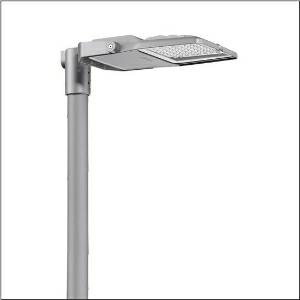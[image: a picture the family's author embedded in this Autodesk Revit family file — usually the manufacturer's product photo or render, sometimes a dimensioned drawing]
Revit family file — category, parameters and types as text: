
# Revit family: floodlight_fl_21_iq_mini___pl43_5xa7772d4a3a_0702
name_source: partatom
category: Lighting Fixtures
units: mm (PartAtom-declared; Revit-internal decimal feet)

## family parameters
Cut with Voids When Loaded = No
Host = Face
Light Source = No
Part Type = Normal
Room Calculation Point = No
Round Connector Dimension = Use Diameter
Shared = No

## types (1)
- --- (1 x LED, 19090 lm, 143 W, 4000K)
    Apparent Load = 143 VA
    CIE Flux Codes = 27 78 99 100 100
    Color Rendering = 70
    Color Temperature = 4000K
    Default Elevation = 1800 mm
    Description = Floodlight FL 21 iQ mini, floodlight, primary light control with lens, of PMMA, primary optical cover: protective disc, of toughened safety glass, transparent, light distribution: PL43, light emission: direct distribution, installation type: surface-mounted, LED, High Power LED, rated luminous flux: 19.090lm, luminous efficacy: 134lm/W, light colour: 740, colour temperature: 4000K, control gear: iQ Street-Remote/DALI, control: Auto-Match, Temp-Guard, Night-Set, Smart-Wire, Desk-Remote (wireless, voltage-free reading and setting of iQ features in the workshop via application-optimized NFC function/RFID function), optimised constant luminous flux control (CLO 2.0), Light-Fading, Lumen-Switch, with terminal, 6-pole, mains connection: 220..240V, AC, 50/60Hz, start of lifetime: 143W, end of service life: 152W, reduction: 61W, luminaire housing, of diecast aluminium, powder-coated, Siteco® metallic grey (DB 702S), corrosivity category C5 mid according to DIN EN ISO 12944, suitable for swimming pools, chlorine-resistant, sealing non-destructively replaceable, please order mast flange separately, mast bracket, of steel, galvanised, powder-coated, protection rating (complete): IP66, insulation class (complete): insulation class II (safety insulation), certification: CE, ENEC, VDE, protection symbol: D, impact resistance: IK08, permissible operating ambient temperature: -40..+40°C, permissible operating ambient temperature for outdoor applications: -40..+50°C, standard: DIN EN 12944, LABS conformity tested according to VDMA 24364:2018-05, packaging unit: 1 piece

Light Distribution: PL43
    Height = 70 mm
    Lamp = 1 x LED
    Lamp Light Flux = 19090 lm
    Lamp Power = 143 W
    Lamp count = 1
    Length = 485 mm
    Luminous efficacy = 133 lm/W
    Manufacturer = Siteco
    ModVariant = No
    Model = 5XA7772D4A3A
    Number of Poles = 1
    OnlyDefault = Yes
    Power Factor = 1
    Product Name = Floodlight FL 21 iQ mini | PL43
    Product group = floodlight | pylon annexe
    ProductGroupID = 6200
    Protection Class = Protection class II
    Protection Degree = IP 66
    RLX_Detail_Level = 1
    RLX_Emergency_Light_Flux = 0 lm
    RLX_Emergency_Type = 0
    RLX_Emergency_Type_DB = No
    RlxData = <blob elided: 101569 chars, md5=c6a1df67>
    Socket = socket
    Standby Power = 0 W
    System Light Flux = 19090 lm
    System Power = 143 W
    Type Comments = factory setting: luminous flux: 100 % | dim-lin: 254 | 730 mA
    Type Image = l_1007125.jpg
    URL = http://relux.com
    VarID = @adj_161474
    Voltage = 0 V
    Weight = 0.00 kg
    Width = 337 mm

## geometry (parser evidence)
native form markers: Blend x4, Sweep x12
no freeform markers — native parametric forms only
